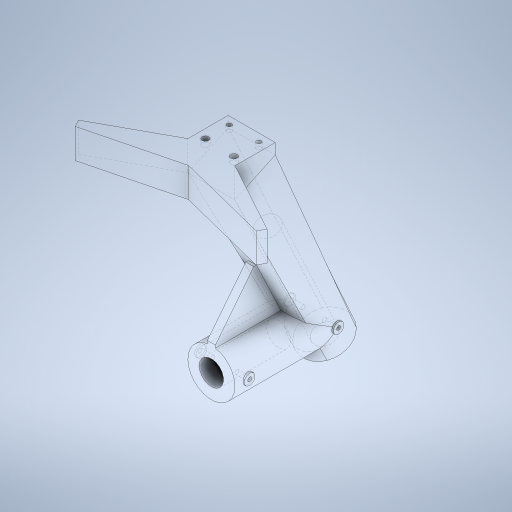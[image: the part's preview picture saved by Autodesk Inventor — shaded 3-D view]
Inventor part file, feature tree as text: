
AUTODESK INVENTOR PART (.ipt)
format: ipt  version: 2023 (Build 270158000, 158)  size: 485,888 bytes
history: native  units: in
note: dims shown in document units (in); Inventor stores cm internally (conversion verified against a paired STEP export)
features: sketch x12, extrude x9, draft x1, plane x1, loft x1, chamfer x1, other x1
ambient origin geometry x8: Origin, YZ Plane, XZ Plane, XY Plane, X Axis, Y Axis, Z Axis, Center Point
bodies: Solid1 (feature_tree)
feature tree (26):
  extrude  "Extrusion1"  Depth=1.1811in
  extrude  "Extrusion2"  Depth=0.2559in
  draft  "FaceDraft1"
  plane  "Work Plane1"
  loft  "Loft1"
  extrude  "Extrusion6"  TaperAngle=0.0deg  [1 undecoded]
  extrude  "Extrusion5"  TaperAngle=0.0deg  [1 undecoded]
  extrude  "Extrusion7"  Depth=0.1575in TaperAngle=0.0deg
  extrude  "Extrusion8"  Depth=0.1718in
  extrude  "Extrusion9"  Depth=1.378in
  extrude  "Extrusion10"  TaperAngle=0.0deg  [1 undecoded]
  chamfer  "Chamfer1"  Distance=3.937in
  sketch  "Sketch12"  dims[d34=0.6299in d35=3.937in d36=0.0in]
  sketch  "Sketch13"  dims[d37=1.378in d38=4.7244in]
  extrude  "Extrusion11"  Depth=4.7244in
  sketch  "Sketch1"  dims[d0=0.1378in d1=0.1969in d2=0.1969in d3=0.1378in d4=1.1811in]
  sketch  "Sketch2"  dims[d5=1.378in d6=0.2559in]
  sketch  "Sketch5"  dims[d7=0.8661in d8=0.7283in]
  other  "Edges1"
  sketch  "Sketch6"  dims[d9=0.0in d10=0.0in]
  sketch  "Sketch7"  dims[d12=0.2264in d13=0.0in]
  sketch  "Sketch8"  dims[d14=0.0in d15=0.1575in d16=0.0in]
  sketch  "Sketch9"  dims[d17=0.1575in d18=0.0in d19=0.1718in]
  sketch  "Sketch10"  dims[d28=6.2992in d29=1.378in]
  sketch  "Sketch11"  dims[d30=0.0in d31=90.0deg d32=0.0in d33=90.0deg]
  sketch  "Sketch15"  dims[d39=0.689in d40=1.378in d41=1.281in d42=0.0in d43=0.7087in d44=1.9685in d45=0.0in d46=0.3937in d47=0.315in d48=0.0787in d49=0.0in d50=0.315in d51=0.0787in d52=0.0in d53=0.1181in d54=0.1181in d55=0.0in d56=0.0in d57=0.0787in d58=0.1181in d59=0.2362in d60=1.5748in d61=1.4272in d62=1.125in d63=45.0deg d64=0.0in d65=2.3622in d66=0.4216in d67=0.2362in d68=90.0deg d69=90.0deg d74=0.8661in d75=0.0in d21=0.0197in d22=0.0344in d23=0.0197in d24=0.0344in]
note: 3 required parameter values undecoded (feature->parameter linkage not recoverable at this tier; creation-order binding heuristic only, values carry confidence <= 0.55)
